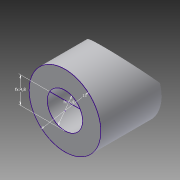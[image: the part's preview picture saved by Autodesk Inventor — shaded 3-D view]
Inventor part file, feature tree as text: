
AUTODESK INVENTOR PART (.ipt)
format: ipt  version: 2013 (Build 170138000, 138)  size: 98,816 bytes
history: native  units: mm
features: extrude x4, sketch x2, projected_geometry x1
ambient origin geometry x8: Origin, YZ Plane, XZ Plane, XY Plane, X Axis, Y Axis, Z Axis, Center Point
bodies: Solid1 (feature_tree)
feature tree (7):
  sketch  "Sketch1"  dims[d0=6.4mm d2=13.0mm]
  extrude  "Extrusion1"  Depth=13.0mm
  extrude  "Extrusion2"  Depth=2.7mm TaperAngle=0.0deg
  extrude  "Extrusion3"  Depth=4.8mm
  extrude  "Extrusion5"  Depth=9.7mm TaperAngle=0.0deg
  sketch  "Sketch3"  dims[d3=11.0mm d4=0.0mm d5=2.7mm d6=0.0mm d7=4.8mm d8=9.7mm d9=0.0mm d12=1.2mm d13=7.0mm d14=10.0mm d15=0.0mm]
  projected_geometry  "Project Cut Edges1"
